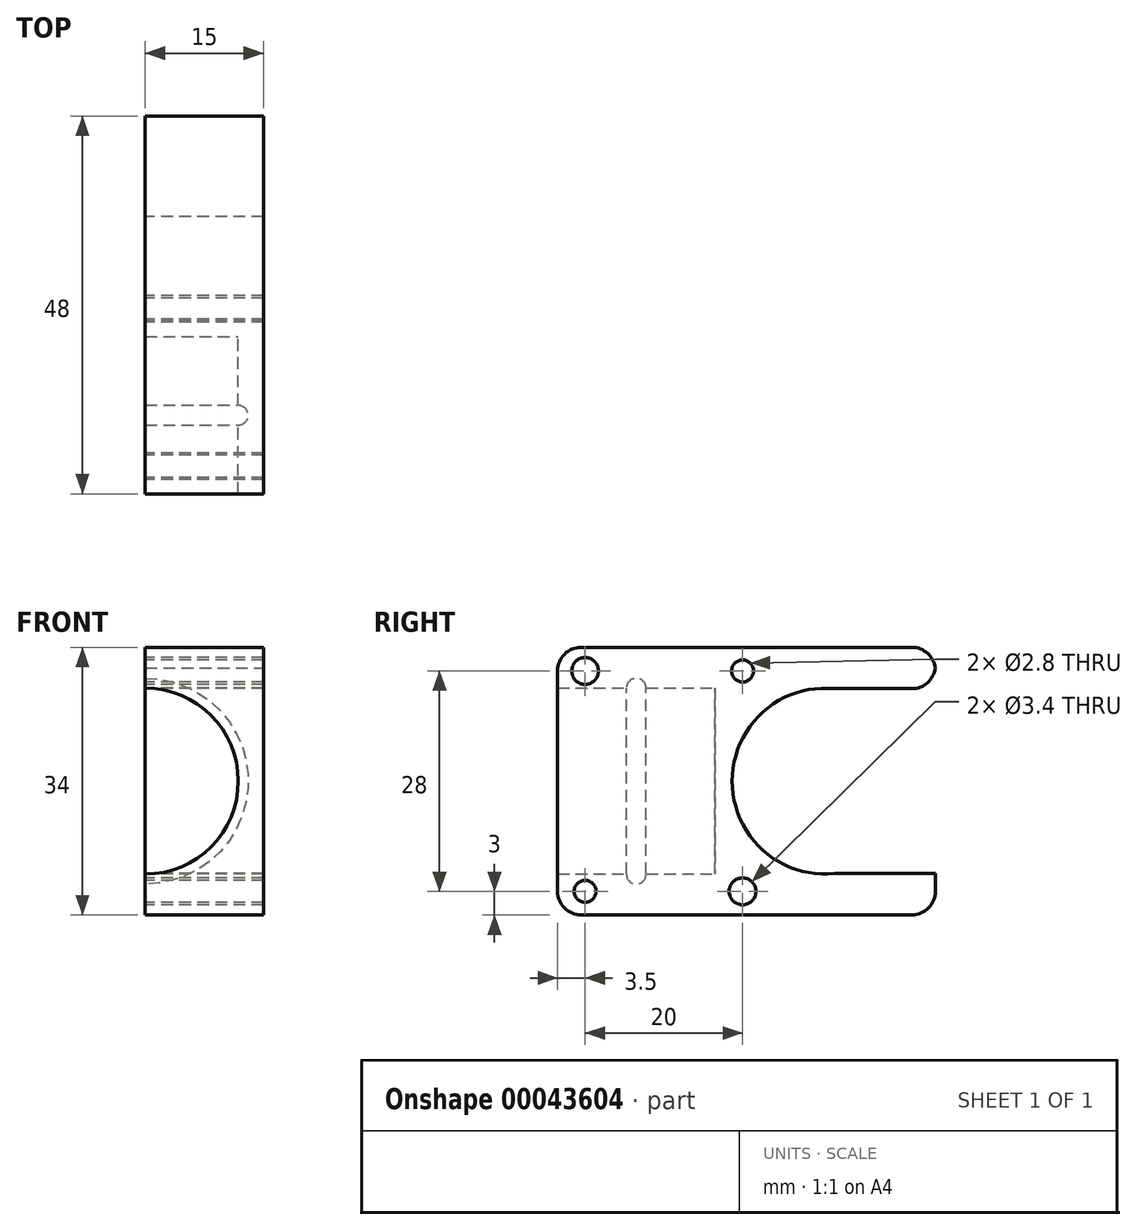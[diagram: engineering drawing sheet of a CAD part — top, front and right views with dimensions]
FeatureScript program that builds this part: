
annotation { "Feature Type Name" : "Feature", "Feature Type Description" : "" }
export const myFeature = defineFeature(function(context is Context, id is Id, definition is map)
    precondition{}
    {
        {
            var Q0;
            Q0=qCreatedBy(makeId("Front.planeOp"),FACE);
            var sketch = newSketch(context, id + "F0", { "sketchPlane" : qUnion([Q0])});
            skLineSegment(sketch, "E0.bottom", {"start": v(0, 17) * mm, "end": v(15, 17) * mm});
            skLineSegment(sketch, "E0.top", {"start": v(0, -17) * mm, "end": v(15, -17) * mm});
            skLineSegment(sketch, "E0.left", {"start": v(0, 17) * mm, "end": v(0, -17) * mm});
            skLineSegment(sketch, "E0.right", {"start": v(15, 17) * mm, "end": v(15, -17) * mm});
            skCircle(sketch, "E1", {"center": v(0, 0) * mm, "radius": 11.8 * mm});
            skPoint(sketch, "E2", {"position": v(0, 14.5) * mm});
            skPoint(sketch, "E3", {"position": v(0, -14.5) * mm});
            skSolve(sketch);
        }
        {
            var Q0;
            {var subQ4=sQuery(id+"F0.wireOp",EDGE,"E0.bottom");Q0=makeQuery(id+"F0.imprint","IMPRINT",FACE,{"disambiguationData":[TD([[makeQuery(id+"F0.imprint","IMPRINT",EDGE,{"derivedFrom":subQ4}),-1.0]])]});}
            extrude(context, id + "F1", {"entities" : qUnion([Q0]), "depth" : 10 * mm, "hasSecondDirection" : true, "secondDirectionOppositeDirection" : true, "secondDirectionDepth" : 10 * mm});
        }
        {
            var Q0;
            {var subQ0=sQuery(id+"F0.wireOp",EDGE,"E0.left");Q0=makeQuery(id+"F1.opExtrude","SWEPT_FACE",FACE,{"disambiguationData":[OSD([subQ0]),TDD([makeQuery(id+"F0.imprint","IMPRINT",EDGE,{"disambiguationData":[TD([[makeQuery(id+"F0.imprint","INTERSECT",VERTEX,{"derivedFrom":[sQuery(id+"F0.wireOp",EDGE,"E0.top"),subQ0]}),1.0]])],"derivedFrom":subQ0})])]});}
            var sketch = newSketch(context, id + "F2", { "sketchPlane" : qUnion([Q0])});
            skPoint(sketch, "E4", {"position": v(-6.5, 14) * mm});
            skPoint(sketch, "E5", {"position": v(6.5, 14) * mm});
            skPoint(sketch, "E6", {"position": v(6.5, -14) * mm});
            skPoint(sketch, "E7", {"position": v(-6.5, -14) * mm});
            skCircle(sketch, "E8", {"center": v(0, -11.8) * mm, "radius": 1.25 * mm});
            skSolve(sketch);
        }
        {
            var Q0;
            {var subQ0=sQuery(id+"F0.wireOp",EDGE,"E0.left");var subQ1=sQuery(id+"F0.wireOp",EDGE,"E1");var subQ2=makeQuery(id+"F1.opExtrude","SWEPT_EDGE",EDGE,{"disambiguationData":[OSD([subQ0,subQ1]),TDD([makeQuery(id+"F0.imprint","INTERSECT",VERTEX,{"disambiguationData":[OD(1.0)],"derivedFrom":[subQ0,subQ1]})])]});var subQ3=sQuery(id+"F2.wireOp",EDGE,"E8");var subQ5=makeQuery(id+"F2.imprint","INTERSECT",VERTEX,{"disambiguationData":[OD(0.0)],"derivedFrom":[subQ2,subQ3]});Q0=makeQuery(id+"F2.imprint","IMPRINT",FACE,{"disambiguationData":[TD([[makeQuery(id+"F2.imprint","IMPRINT",EDGE,{"disambiguationData":[TD([[subQ5,-1.0]])],"derivedFrom":subQ3}),1.0]])]});}
            var Q1;
            Q1=sQuery(id+"F0.wireOp",EDGE,"E1");
            revolve(context, id + "F3", {"operationType" : NewBodyOperationType.REMOVE, "entities" : qUnion([Q0]), "axis" : qUnion([Q1]), "revolveType" : RevolveType.FULL, "oppositeDirection" : true});
        }
        {
            var Q0;
            Q0=makeQuery(id+"F1.opExtrude","CAP_FACE",FACE,{"disambiguationData":[OSD([sQuery(id+"F0.wireOp",EDGE,"E0.bottom"),sQuery(id+"F0.wireOp",EDGE,"E0.top"),sQuery(id+"F0.wireOp",EDGE,"E0.left"),sQuery(id+"F0.wireOp",EDGE,"E0.right"),sQuery(id+"F0.wireOp",EDGE,"E1")])],"isStart":true});
            var sketch = newSketch(context, id + "F4", { "sketchPlane" : qUnion([Q0])});
            skLineSegment(sketch, "E9.bottom", {"start": v(-15, 17) * mm, "end": v(0, 17) * mm});
            skLineSegment(sketch, "E9.top", {"start": v(-15, -17) * mm, "end": v(0, -17) * mm});
            skLineSegment(sketch, "E9.left", {"start": v(-15, 17) * mm, "end": v(-15, -17) * mm});
            skLineSegment(sketch, "E9.right", {"start": v(0, 17) * mm, "end": v(0, -17) * mm});
            skSolve(sketch);
        }
        {
            var Q0;
            {var subQ0=makeQuery(id+"F1.opExtrude","CAP_EDGE",EDGE,{"disambiguationData":[OSD([sQuery(id+"F0.wireOp",EDGE,"E1")])],"isStart":true});Q0=makeQuery(id+"F4.imprint","IMPRINT",FACE,{"disambiguationData":[TD([[makeQuery(id+"F4.imprint","IMPRINT",EDGE,{"derivedFrom":subQ0}),-1.0]])]});}
            var Q1;
            {var subQ3=sQuery(id+"F4.wireOp",EDGE,"E9.bottom");Q1=makeQuery(id+"F4.imprint","IMPRINT",FACE,{"disambiguationData":[TD([[makeQuery(id+"F4.imprint","IMPRINT",EDGE,{"derivedFrom":subQ3}),1.0]])]});}
            extrude(context, id + "F5", {"entities" : qUnion([Q0, Q1]), "depth" : 28 * mm});
        }
        {
            var Q0;
            Q0=makeQuery(id+"F1.opExtrude","SWEPT_BODY",BODY,{"disambiguationData":[OSD([sQuery(id+"F0.wireOp",EDGE,"E0.bottom"),sQuery(id+"F0.wireOp",EDGE,"E0.top"),sQuery(id+"F0.wireOp",EDGE,"E0.left"),sQuery(id+"F0.wireOp",EDGE,"E0.right"),sQuery(id+"F0.wireOp",EDGE,"E1")])]});
            var Q1;
            Q1=makeQuery(id+"F5.opExtrude","SWEPT_BODY",BODY,{"disambiguationData":[OSD([sQuery(id+"F4.wireOp",EDGE,"E9.bottom"),sQuery(id+"F4.wireOp",EDGE,"E9.top"),sQuery(id+"F4.wireOp",EDGE,"E9.left"),sQuery(id+"F4.wireOp",EDGE,"E9.right")])]});
            booleanBodies(context, id + "F6", {"operationType" : BooleanOperationType.UNION, "tools" : qUnion([Q0, Q1])});
        }
        {
            var Q0;
            {var subQ0=sQuery(id+"F0.wireOp",EDGE,"E0.left");Q0=makeQuery(id+"F6.opBoolean","MERGE",FACE,{"derivedFrom":[makeQuery(id+"F1.opExtrude","SWEPT_FACE",FACE,{"disambiguationData":[OSD([subQ0]),TDD([makeQuery(id+"F0.imprint","IMPRINT",EDGE,{"disambiguationData":[TD([[makeQuery(id+"F0.imprint","INTERSECT",VERTEX,{"derivedFrom":[sQuery(id+"F0.wireOp",EDGE,"E0.bottom"),subQ0]}),-1.0]])],"derivedFrom":subQ0})])]}),makeQuery(id+"F1.opExtrude","SWEPT_FACE",FACE,{"disambiguationData":[OSD([subQ0]),TDD([makeQuery(id+"F0.imprint","IMPRINT",EDGE,{"disambiguationData":[TD([[makeQuery(id+"F0.imprint","INTERSECT",VERTEX,{"derivedFrom":[sQuery(id+"F0.wireOp",EDGE,"E0.top"),subQ0]}),1.0]])],"derivedFrom":subQ0})])]}),makeQuery(id+"F5.opExtrude","SWEPT_FACE",FACE,{"disambiguationData":[OSD([sQuery(id+"F4.wireOp",EDGE,"E9.right")])]})]});}
            var sketch = newSketch(context, id + "F7", { "sketchPlane" : qUnion([Q0])});
            skPoint(sketch, "E10", {"position": v(-24, 0) * mm});
            skPoint(sketch, "E11", {"position": v(-34.5, 14) * mm});
            skPoint(sketch, "E12", {"position": v(-13.5, 14) * mm});
            skPoint(sketch, "E13", {"position": v(-13.5, -14) * mm});
            skPoint(sketch, "E14", {"position": v(-34.5, -14) * mm});
            skLineSegment(sketch, "E15.bottom", {"start": v(-38, -11.75) * mm, "end": v(-24, -11.75) * mm});
            skLineSegment(sketch, "E15.top", {"start": v(-38, 11.75) * mm, "end": v(-24, 11.75) * mm});
            skLineSegment(sketch, "E15.left", {"start": v(-38, -11.75) * mm, "end": v(-38, 11.75) * mm});
            skLineSegment(sketch, "E15.right", {"start": v(-24, -11.75) * mm, "end": v(-24, 11.75) * mm});
            skSolve(sketch);
        }
        {
            var Q0;
            Q0=sQuery(id+"F7.wireOp",VERTEX,"E10");
            var Q1;
            Q1=makeQuery(id+"F1.opExtrude","SWEPT_BODY",BODY,{"disambiguationData":[OSD([sQuery(id+"F0.wireOp",EDGE,"E0.bottom"),sQuery(id+"F0.wireOp",EDGE,"E0.top"),sQuery(id+"F0.wireOp",EDGE,"E0.left"),sQuery(id+"F0.wireOp",EDGE,"E0.right"),sQuery(id+"F0.wireOp",EDGE,"E1")])]});
            hole(context, id + "F8", {"style" : HoleStyle.SIMPLE, "holeDiameter" : 23.62 * mm, "endStyle" : HoleEndStyle.THROUGH, "locations" : qUnion([Q0]), "scope" : qUnion([Q1])});
        }
        {
            var Q0;
            Q0=sQuery(id+"F7.wireOp",VERTEX,"E12");
            var Q1;
            Q1=sQuery(id+"F2.wireOp",VERTEX,"E6");
            var Q2;
            Q2=makeQuery(id+"F1.opExtrude","SWEPT_BODY",BODY,{"disambiguationData":[OSD([sQuery(id+"F0.wireOp",EDGE,"E0.bottom"),sQuery(id+"F0.wireOp",EDGE,"E0.top"),sQuery(id+"F0.wireOp",EDGE,"E0.left"),sQuery(id+"F0.wireOp",EDGE,"E0.right"),sQuery(id+"F0.wireOp",EDGE,"E1")])]});
            hole(context, id + "F9", {"style" : HoleStyle.SIMPLE, "holeDiameter" : 2.8 * mm, "endStyle" : HoleEndStyle.THROUGH, "locations" : qUnion([Q0, Q1]), "scope" : qUnion([Q2])});
        }
        {
            var Q0;
            Q0=sQuery(id+"F7.wireOp",VERTEX,"E13");
            var Q1;
            Q1=sQuery(id+"F2.wireOp",VERTEX,"E5");
            var Q2;
            Q2=makeQuery(id+"F1.opExtrude","SWEPT_BODY",BODY,{"disambiguationData":[OSD([sQuery(id+"F0.wireOp",EDGE,"E0.bottom"),sQuery(id+"F0.wireOp",EDGE,"E0.top"),sQuery(id+"F0.wireOp",EDGE,"E0.left"),sQuery(id+"F0.wireOp",EDGE,"E0.right"),sQuery(id+"F0.wireOp",EDGE,"E1")])]});
            hole(context, id + "F10", {"style" : HoleStyle.SIMPLE, "holeDiameter" : 3.4 * mm, "endStyle" : HoleEndStyle.THROUGH, "locations" : qUnion([Q0, Q1]), "scope" : qUnion([Q2])});
        }
        {
            var Q0;
            Q0=makeQuery(id+"F7.imprint","IMPRINT",FACE,{"disambiguationData":[TD([[makeQuery(id+"F7.imprint","IMPRINT",EDGE,{"derivedFrom":sQuery(id+"F7.wireOp",EDGE,"E15.bottom")}),1.0]])]});
            extrude(context, id + "F11", {"entities" : qUnion([Q0]), "operationType" : NewBodyOperationType.REMOVE, "oppositeDirection" : true, "depth" : 25 * mm});
        }
        {
            var Q0;
            Q0=makeQuery(id+"F1.opExtrude","CAP_EDGE",EDGE,{"disambiguationData":[OSD([sQuery(id+"F0.wireOp",EDGE,"E0.top")])],"isStart":false});
            var Q1;
            Q1=makeQuery(id+"F1.opExtrude","CAP_EDGE",EDGE,{"disambiguationData":[OSD([sQuery(id+"F0.wireOp",EDGE,"E0.bottom")])],"isStart":false});
            var Q2;
            Q2=makeQuery(id+"F5.opExtrude","CAP_EDGE",EDGE,{"disambiguationData":[OSD([sQuery(id+"F4.wireOp",EDGE,"E9.top")])],"isStart":false});
            var Q3;
            Q3=makeQuery(id+"F5.opExtrude","CAP_EDGE",EDGE,{"disambiguationData":[OSD([sQuery(id+"F4.wireOp",EDGE,"E9.bottom")])],"isStart":false});
            var Q4;
            Q4=makeQuery(id+"F11.boolean.opBoolean","COPY",EDGE,{"derivedFrom":makeQuery(id+"F11.opExtrude","SWEPT_EDGE",EDGE,{"disambiguationData":[OSD([sQuery(id+"F4.wireOp",EDGE,"E9.right"),sQuery(id+"F7.wireOp",EDGE,"E15.bottom"),sQuery(id+"F7.wireOp",EDGE,"E15.left")])]})});
            var Q5;
            Q5=makeQuery(id+"F11.boolean.opBoolean","COPY",EDGE,{"derivedFrom":makeQuery(id+"F11.opExtrude","SWEPT_EDGE",EDGE,{"disambiguationData":[OSD([sQuery(id+"F4.wireOp",EDGE,"E9.right"),sQuery(id+"F7.wireOp",EDGE,"E15.top"),sQuery(id+"F7.wireOp",EDGE,"E15.left")])]})});
            fillet(context, id + "F12", {"entities" : qUnion([Q0, Q1, Q2, Q3, Q4, Q5]), "radius" : 3 * mm, "tangentPropagation" : true, "allowEdgeOverflow" : false});
        }
    });
